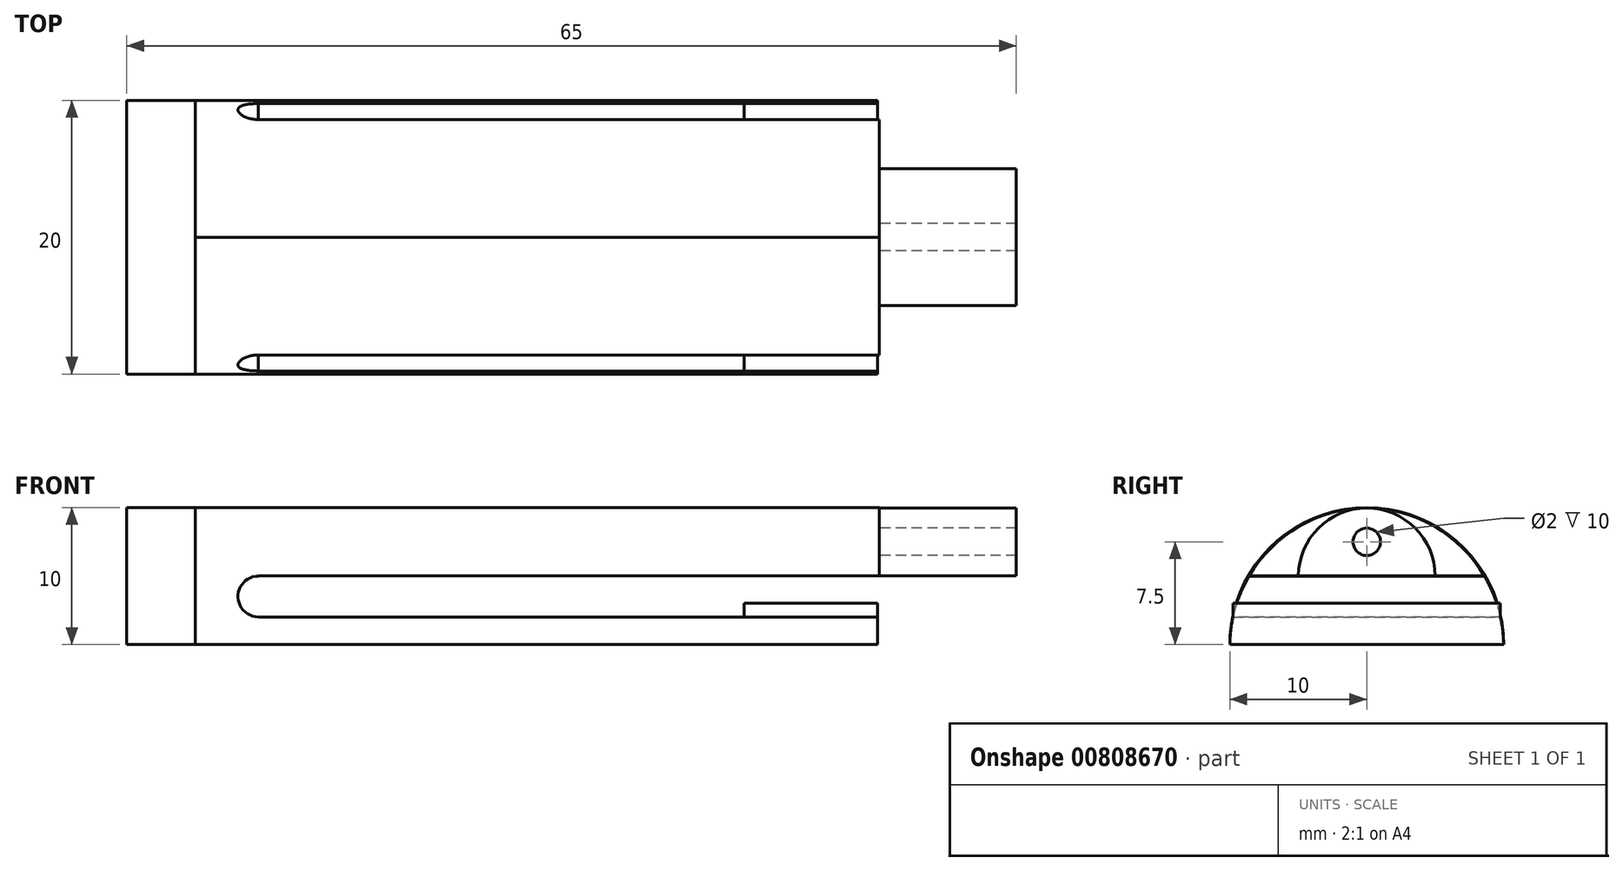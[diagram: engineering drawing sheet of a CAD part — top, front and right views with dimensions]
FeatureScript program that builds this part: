
annotation { "Feature Type Name" : "Feature", "Feature Type Description" : "" }
export const myFeature = defineFeature(function(context is Context, id is Id, definition is map)
    precondition{}
    {
        {
            var Q0;
            Q0=qCreatedBy(makeId("Top.planeOp"),FACE);
            var sketch = newSketch(context, id + "F0", { "sketchPlane" : qUnion([Q0])});
            skLineSegment(sketch, "E0.bottom", {"start": v(25, 10) * mm, "end": v(-25, 10) * mm});
            skLineSegment(sketch, "E0.top", {"start": v(25, -10) * mm, "end": v(-25, -10) * mm});
            skLineSegment(sketch, "E0.left", {"start": v(25, 10) * mm, "end": v(25, -10) * mm});
            skLineSegment(sketch, "E0.right", {"start": v(-25, 10) * mm, "end": v(-25, -10) * mm});
            skPoint(sketch, "E0.middle", {"position": v(0, 0) * mm});
            skPoint(sketch, "E1.middle", {"position": v(25, 0) * mm});
            skLineSegment(sketch, "E2", {"start": v(25, 1.31) * mm, "end": v(25, -1.31) * mm});
            skLineSegment(sketch, "E3", {"start": v(25, -1.31) * mm, "end": v(25, 1.31) * mm});
            skSolve(sketch);
        }
        {
            var Q0;
            {var subQ5=sQuery(id+"F0.wireOp",EDGE,"E1.left");Q0=makeQuery(id+"F0.imprint","IMPRINT",FACE,{"disambiguationData":[TD([[makeQuery(id+"F0.imprint","IMPRINT",EDGE,{"derivedFrom":subQ5}),1.0]])]});}
            var Q1;
            {var subQ5=sQuery(id+"F0.wireOp",EDGE,"E1.right");Q1=makeQuery(id+"F0.imprint","IMPRINT",FACE,{"disambiguationData":[TD([[makeQuery(id+"F0.imprint","IMPRINT",EDGE,{"derivedFrom":subQ5}),-1.0]])]});}
            var Q2;
            {var subQ4=sQuery(id+"F0.wireOp",EDGE,"E0.bottom");Q2=makeQuery(id+"F0.imprint","IMPRINT",FACE,{"disambiguationData":[TD([[makeQuery(id+"F0.imprint","IMPRINT",EDGE,{"derivedFrom":subQ4}),1.0]])]});}
            var Q3;
            Q3=makeQuery(id+"F0.imprint","IMPRINT",FACE,{"disambiguationData":[TD([[makeQuery(id+"F0.imprint","IMPRINT",EDGE,{"derivedFrom":sQuery(id+"F0.wireOp",EDGE,"E3")}),-1.0]])]});
            extrude(context, id + "F1", {"entities" : qUnion([Q0, Q1, Q2, Q3]), "depth" : 5 * mm, "offsetDistance" : 25.4 * mm});
        }
        {
            var Q0;
            Q0=makeQuery(id+"F1.opExtrude","SWEPT_FACE",FACE,{"disambiguationData":[OSD([sQuery(id+"F0.wireOp",EDGE,"E0.left"),sQuery(id+"F0.wireOp",EDGE,"E3")])]});
            var sketch = newSketch(context, id + "F2", { "sketchPlane" : qUnion([Q0])});
            skCircle(sketch, "E4", {"center": v(0, 2.5) * mm, "radius": 1 * mm});
            skPoint(sketch, "E4.centerSnap0", {"position": v(-10, 2.5) * mm});
            skLineSegment(sketch, "E5", {"start": v(0, 0) * mm, "end": v(-5, 0) * mm});
            skLineSegment(sketch, "E6", {"start": v(0, 0) * mm, "end": v(5, 0) * mm});
            skArc(sketch, "E7", {"start": v(5, 0) * mm, "mid": v(0, 4.97) * mm, "end": v(-5, 0) * mm});
            skSolve(sketch);
        }
        {
            var Q0;
            Q0=makeQuery(id+"F2.imprint","IMPRINT",FACE,{"disambiguationData":[TD([[makeQuery(id+"F2.imprint","IMPRINT",EDGE,{"derivedFrom":sQuery(id+"F2.wireOp",EDGE,"E4")}),-1.0]])]});
            extrude(context, id + "F3", {"entities" : qUnion([Q0]), "operationType" : NewBodyOperationType.ADD, "depth" : 10 * mm, "offsetDistance" : 25.4 * mm});
        }
        {
            var Q0;
            Q0=makeQuery(id+"F1.opExtrude","SWEPT_FACE",FACE,{"disambiguationData":[OSD([sQuery(id+"F0.wireOp",EDGE,"E0.bottom")])]});
            var sketch = newSketch(context, id + "F4", { "sketchPlane" : qUnion([Q0])});
            skLineSegment(sketch, "E8", {"start": v(25, 0) * mm, "end": v(25, -5) * mm});
            skLineSegment(sketch, "E9", {"start": v(20.38, 0) * mm, "end": v(20.38, -5) * mm});
            skLineSegment(sketch, "E10", {"start": v(20.38, -5) * mm, "end": v(25, -5) * mm});
            skLineSegment(sketch, "E11", {"start": v(20.38, -5) * mm, "end": v(-24.87, -5) * mm});
            skLineSegment(sketch, "E12", {"start": v(-24.87, -5) * mm, "end": v(-24.87, -3) * mm});
            skLineSegment(sketch, "E13", {"start": v(20.38, -2.5) * mm, "end": v(20.38, -5) * mm});
            skLineSegment(sketch, "E14", {"start": v(-24.87, -3) * mm, "end": v(20.38, -3) * mm});
            skSolve(sketch);
        }
        {
            var Q0;
            Q0 = qSketchRegion(id + "F4", true);
            var Q1;
            {var subQ6=sQuery(id+"F4.wireOp",EDGE,"E8");Q1=makeQuery(id+"F4.imprint","IMPRINT",FACE,{"disambiguationData":[TD([[makeQuery(id+"F4.imprint","IMPRINT",EDGE,{"derivedFrom":subQ6}),-1.0]])]});}
            extrude(context, id + "F5", {"entities" : qUnion([Q0, Q1]), "oppositeDirection" : true, "depth" : 20 * mm, "offsetDistance" : 25.4 * mm});
        }
        {
            var Q0;
            Q0=makeQuery(id+"F5.opExtrude","CAP_FACE",FACE,{"disambiguationData":[OSD([sQuery(id+"F0.wireOp",EDGE,"E0.bottom"),sQuery(id+"F4.wireOp",EDGE,"E8"),sQuery(id+"F4.wireOp",EDGE,"E9"),sQuery(id+"F4.wireOp",EDGE,"E10"),sQuery(id+"F4.wireOp",EDGE,"E11"),sQuery(id+"F4.wireOp",EDGE,"E12"),sQuery(id+"F4.wireOp",EDGE,"YV0F7N8K-6bOk-KfLq-WGGl-ljcRE3S60Gok")])],"isStart":true});
            var sketch = newSketch(context, id + "F6", { "sketchPlane" : qUnion([Q0])});
            skCircle(sketch, "E15", {"center": v(20.38, -1.5) * mm, "radius": 1.5 * mm});
            skSolve(sketch);
        }
        {
            var Q0;
            Q0 = qSketchRegion(id + "F6", true);
            extrude(context, id + "F7", {"entities" : qUnion([Q0]), "operationType" : NewBodyOperationType.REMOVE, "oppositeDirection" : true, "depth" : 20 * mm, "offsetDistance" : 25.4 * mm});
        }
        {
            var Q0;
            Q0=makeQuery(id+"F5.opExtrude","SWEPT_BODY",BODY,{"disambiguationData":[OSD([sQuery(id+"F0.wireOp",EDGE,"E0.bottom"),sQuery(id+"F4.wireOp",EDGE,"E8"),sQuery(id+"F4.wireOp",EDGE,"E9"),sQuery(id+"F4.wireOp",EDGE,"E10"),sQuery(id+"F4.wireOp",EDGE,"E11"),sQuery(id+"F4.wireOp",EDGE,"E12"),sQuery(id+"F4.wireOp",EDGE,"E13"),sQuery(id+"F4.wireOp",EDGE,"E14")])]});
            var Q1;
            Q1=makeQuery(id+"F1.opExtrude","SWEPT_BODY",BODY,{"disambiguationData":[OSD([sQuery(id+"F0.wireOp",EDGE,"E0.bottom"),sQuery(id+"F0.wireOp",EDGE,"E0.top"),sQuery(id+"F0.wireOp",EDGE,"E0.left"),sQuery(id+"F0.wireOp",EDGE,"E0.right"),sQuery(id+"F0.wireOp",EDGE,"E3")])]});
            booleanBodies(context, id + "F8", {"operationType" : BooleanOperationType.UNION, "tools" : qUnion([Q0, Q1])});
        }
        {
            var Q0;
            Q0=makeQuery(id+"F1.opExtrude","CAP_EDGE",EDGE,{"disambiguationData":[OSD([sQuery(id+"F0.wireOp",EDGE,"E0.top")])],"isStart":false});
            var Q1;
            Q1=makeQuery(id+"F1.opExtrude","CAP_EDGE",EDGE,{"disambiguationData":[OSD([sQuery(id+"F0.wireOp",EDGE,"E0.bottom")])],"isStart":false});
            fillet(context, id + "F9", {"entities" : qUnion([Q0, Q1]), "radius" : 10.16 * mm, "tangentPropagation" : true, "allowEdgeOverflow" : false});
        }
        {
            var Q0;
            Q0=makeQuery(id+"F5.opExtrude","SWEPT_FACE",FACE,{"disambiguationData":[OSD([sQuery(id+"F4.wireOp",EDGE,"E14")])]});
            var sketch = newSketch(context, id + "F10", { "sketchPlane" : qUnion([Q0])});
            skLineSegment(sketch, "E16", {"start": v(24.87, -9.77) * mm, "end": v(24.87, 9.77) * mm});
            skLineSegment(sketch, "E17", {"start": v(15.11, 9.77) * mm, "end": v(15.11, -9.77) * mm});
            skLineSegment(sketch, "E18", {"start": v(15.11, -9.77) * mm, "end": v(24.87, -9.77) * mm});
            skLineSegment(sketch, "E19", {"start": v(15.11, 9.77) * mm, "end": v(24.87, 9.77) * mm});
            skSolve(sketch);
        }
        {
            var Q0;
            Q0 = qSketchRegion(id + "F10", true);
            extrude(context, id + "F11", {"entities" : qUnion([Q0]), "operationType" : NewBodyOperationType.ADD, "depth" : 1 * mm, "offsetDistance" : 25.4 * mm});
        }
        {
            var Q0;
            Q0=makeQuery(id+"F8.opBoolean","MERGE",FACE,{"derivedFrom":[makeQuery(id+"F1.opExtrude","SWEPT_FACE",FACE,{"disambiguationData":[OSD([sQuery(id+"F0.wireOp",EDGE,"E0.right")])]}),makeQuery(id+"F5.opExtrude","SWEPT_FACE",FACE,{"disambiguationData":[OSD([sQuery(id+"F4.wireOp",EDGE,"E8")])]})]});
            var sketch = newSketch(context, id + "F12", { "sketchPlane" : qUnion([Q0])});
            skLineSegment(sketch, "E20", {"start": v(-10, -5) * mm, "end": v(10, -5) * mm});
            skArc(sketch, "E21", {"start": v(10, -5) * mm, "mid": v(0, 5) * mm, "end": v(-10, -5) * mm});
            skSolve(sketch);
        }
        {
            var Q0;
            Q0 = qSketchRegion(id + "F12", true);
            extrude(context, id + "F13", {"entities" : qUnion([Q0]), "operationType" : NewBodyOperationType.ADD, "depth" : 5 * mm, "offsetDistance" : 25.4 * mm});
        }
    });
